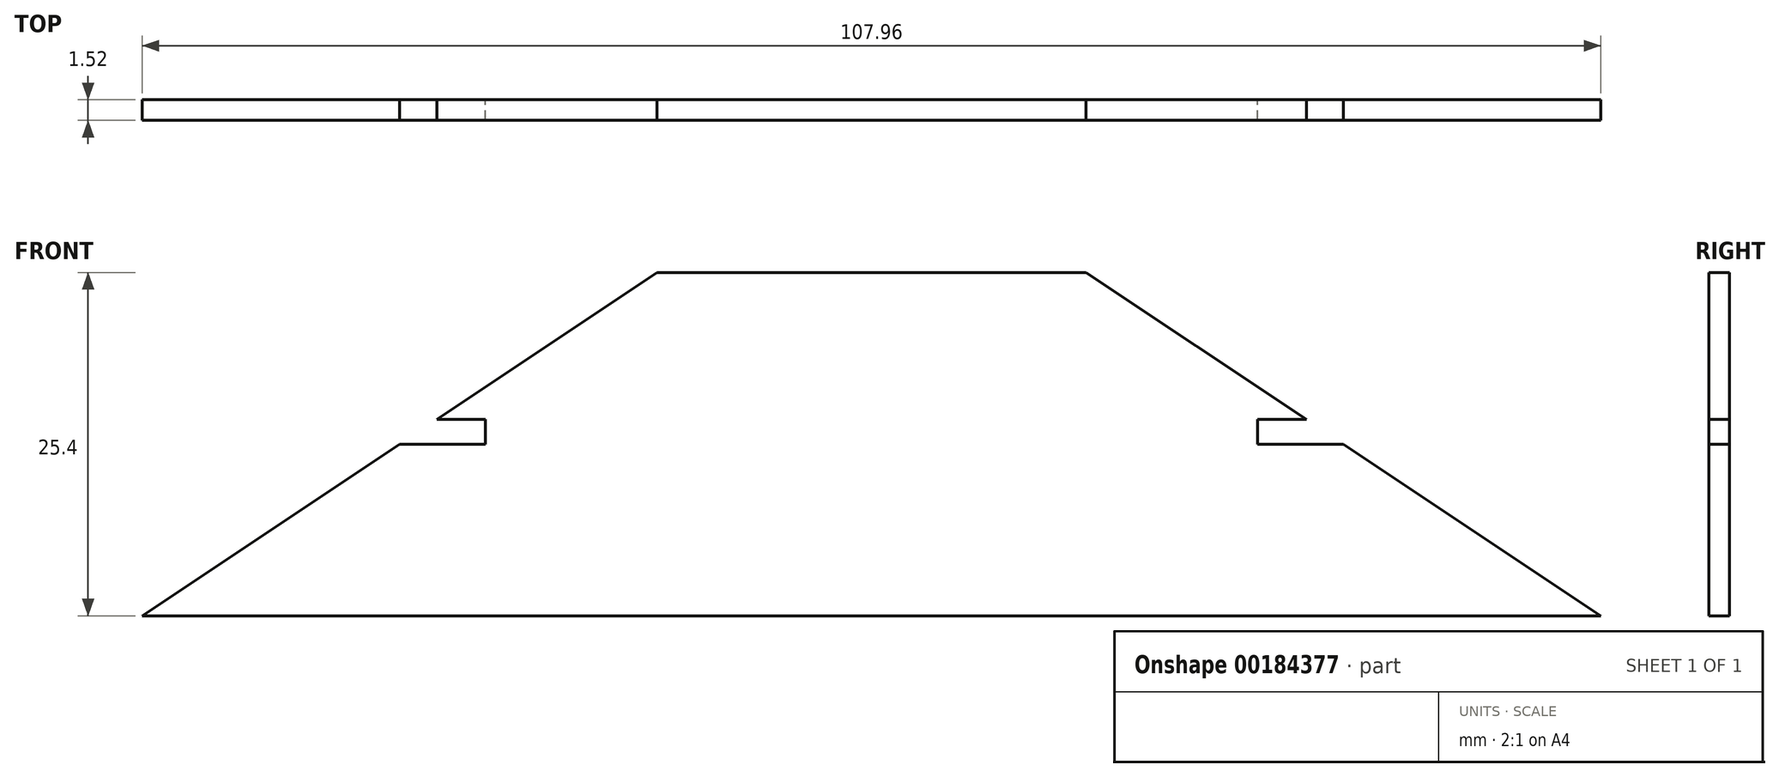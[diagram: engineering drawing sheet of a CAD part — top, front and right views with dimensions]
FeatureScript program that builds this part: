
annotation { "Feature Type Name" : "Feature", "Feature Type Description" : "" }
export const myFeature = defineFeature(function(context is Context, id is Id, definition is map)
    precondition{}
    {
        {
            var Q0;
            Q0=qCreatedBy(makeId("Front.planeOp"),FACE);
            var sketch = newSketch(context, id + "F0", { "sketchPlane" : qUnion([Q0])});
            skLineSegment(sketch, "E0", {"start": v(-15.87, 25.4) * mm, "end": v(15.87, 25.4) * mm});
            skLineSegment(sketch, "E1", {"start": v(15.87, 25.4) * mm, "end": v(53.97, 0) * mm});
            skLineSegment(sketch, "E2", {"start": v(53.97, 0) * mm, "end": v(-53.97, 0) * mm});
            skLineSegment(sketch, "E3", {"start": v(-53.98, 0) * mm, "end": v(-15.87, 25.4) * mm});
            skLineSegment(sketch, "E4", {"start": v(-32.18, 14.53) * mm, "end": v(-28.57, 14.53) * mm});
            skLineSegment(sketch, "E5", {"start": v(-28.57, 14.53) * mm, "end": v(-28.57, 12.7) * mm});
            skLineSegment(sketch, "E6", {"start": v(-28.57, 12.7) * mm, "end": v(-34.92, 12.7) * mm});
            skLineSegment(sketch, "E7", {"start": v(32.18, 14.53) * mm, "end": v(28.57, 14.53) * mm});
            skLineSegment(sketch, "E8", {"start": v(28.57, 14.53) * mm, "end": v(28.57, 12.7) * mm});
            skLineSegment(sketch, "E9", {"start": v(28.57, 12.7) * mm, "end": v(34.92, 12.7) * mm});
            skLineSegment(sketch, "E10", {"start": v(-28.57, 12.7) * mm, "end": v(28.57, 12.7) * mm, "construction": true});
            skLineSegment(sketch, "E11", {"start": v(0, 25.4) * mm, "end": v(0, 0) * mm, "construction": true});
            skSolve(sketch);
        }
        {
            var Q0;
            {var subQ2=sQuery(id+"F0.wireOp",EDGE,"E0");Q0=makeQuery(id+"F0.imprint","IMPRINT",FACE,{"disambiguationData":[TD([[makeQuery(id+"F0.imprint","IMPRINT",EDGE,{"derivedFrom":subQ2}),-1.0]])]});}
            extrude(context, id + "F1", {"entities" : qUnion([Q0]), "depth" : 1.52 * mm});
        }
    });
